# Revit family: LUXI_WATERPROOF LIGHT_HP-E
name_source: partatom
category: Apparecchi per illuminazione
revit_build: Autodesk Revit 2016 (Build: 20161004_0715(x64)
units: mm (PartAtom-declared; Revit-internal decimal feet)

## family parameters
Condiviso = No
Host = Superficie
Numero OmniClass = 23.80.70.00
Punto di calcolo locali = Sì
Quota connettore circolare = Usa diametro
Sorgente d'illuminazione = Sì
Taglio con vuoti quando caricato = No
Tipo di parte = Normale
Titolo OmniClass = Lighting

## types (10) — shared parameters
Alimentatore = Incluso
Alimentazione = 220-240V AC / 50-60 Hz
Angolo inclinazione = -90.00°
Certificazioni = CE / RohS
Classe di efficienza energetica = A+
Classe di protezione = I
Classe di rischio fotobiologico = Esente (RG0)
Colore = Grigio
Descrizione = Plafoniera Standard
Fattore di correzione di potenza = ≥0,95 (typ.)
Filtro dei colori = 16777215
Garanzia = 5 anni
Grado di protezione = IP 65 (frontale)
IFCExportAs = IfcLightFixtureType
Indice di resa cromatica = ≥80 (typ.)
Masterformat 2016 Codice = 26.50.00
Masterformat 2016 Descrizione = Lighting
Materiale 1 = Policarbonato V2_Grigio
Materiale 2 = Policarbonato V2 Diffondente
Materiale 3 = Policarbonato
Modello = Serie HP-E | Waterproof Light
Ottiche = Schermo policarbonato opalino riflettente
Produttore = Luxi Illuminazione S.r.l.
Prospetto di default = 2000 mm  [stored 6.56168 ft]
Protezione agli urti = IK10 (20 Joule)
Regolazione del flusso luminoso = Non disponibile
Rendi la forma visibile nel rendering = No
Revisione = 3
Sistema di illuminazione = Luce diretta
Sorgente = LED SMD
Step MacAdam (SDCM) = <4
Temperatura di esercizio = -40°C / +40°C
Tipologie di installazione = Sospensione / Parete / Soffitto
URL = https://www.luxi.lighting
Uniclass 2015 Codice = EF_70_80
Uniclass 2015 Descrizione = Lighting
Variazione temperatura colore lampada con luminosità attenuata = <Nessuno>
Vita utile = L70B20 50.000ore

## per-type parameters (varying)
| type | Carico apparente | Commenti sul tipo | Dimensioni | Emetti da larghezza rettangolo | Emetti da lunghezza rettangolo | File diagramma fotometrico | H | Larghezza | Lunghezza | Mod.1 | Mod.2 | Nota chiave | Peso | Potenza |
| WPHP020602G840 | 20 VA |  | 620x75x100 | 100 mm  [stored 0.328084 ft] | 620 mm  [stored 2.03412 ft] | WPHP020602G840 Luxi Serie HP-E 20W 4000K 600mm.IES | 75 mm | 100 mm  [stored 0.328084 ft] | 620 mm  [stored 2.03412 ft] | Sì | No |  | 1.20 kg | 20 W |
| WPHP040122G840 | 40 VA |  | 1220x75x100 | 100 mm  [stored 0.328084 ft] | 1220 mm  [stored 4.00262 ft] | WPHP040122G840 Luxi Serie HP-E 40W 4000K 1200mm.IES | 75 mm | 100 mm  [stored 0.328084 ft] | 1220 mm  [stored 4.00262 ft] | Sì | No |  | 2.20 kg | 40 W |
| WPHP030152G840 | 30 VA |  | 1520x75x100 | 100 mm  [stored 0.328084 ft] | 1520 mm | WPHP030152G840 Luxi Serie HP-E 30W 4000K 1500mm.IES | 75 mm | 100 mm  [stored 0.328084 ft] | 1520 mm | Sì | No |  | 2.80 kg | 30 W |
| WPHP060152G840 | 60 VA |  | 1520x75x100 | 100 mm  [stored 0.328084 ft] | 1520 mm | WPHP060152G840 Luxi Serie HP-E 60W 4000K 1500mm.IES | 75 mm | 100 mm  [stored 0.328084 ft] | 1520 mm | Sì | No |  | 2.80 kg | 60 W |
| WPHP060152G840P | 60 VA | Passante | 1520x75x100 | 100 mm  [stored 0.328084 ft] | 1520 mm | WPHP060152G840 Luxi Serie HP-E 60W 4000K 1500mm.IES | 75 mm | 100 mm  [stored 0.328084 ft] | 1520 mm | Sì | No |  | 2.80 kg | 60 W |
| WPHP020602G840E | 20 VA | Emergenza | 620x75x100 | 100 mm  [stored 0.328084 ft] | 620 mm  [stored 2.03412 ft] | WPHP020602G840 Luxi Serie HP-E 20W 4000K 600mm.IES | 75 mm | 100 mm  [stored 0.328084 ft] | 620 mm  [stored 2.03412 ft] | Sì | No | Autonomia 1h, ricarica 12h, SA 12W / 1400 lumen | 1.60 kg | 20 W |
| WPHP030152G840E | 30 VA | Emergenza | 1520x75x100 | 100 mm  [stored 0.328084 ft] | 1520 mm | WPHP030152G840 Luxi Serie HP-E 30W 4000K 1500mm.IES | 75 mm | 100 mm  [stored 0.328084 ft] | 1520 mm | Sì | No | Autonomia 1h, ricarica 12h, SA 12W / 1400 lumen | 3.20 kg | 30 W |
| WPHP040122G840E | 40 VA | Emergenza | 1220x75x100 | 100 mm  [stored 0.328084 ft] | 1220 mm  [stored 4.00262 ft] | WPHP040122G840 Luxi Serie HP-E 40W 4000K 1200mm.IES | 75 mm | 100 mm  [stored 0.328084 ft] | 1220 mm  [stored 4.00262 ft] | Sì | No | Autonomia 1h, ricarica 12h, SA 12W / 1400 lumen | 2.60 kg | 40 W |
| WPHP060152G840E | 60 VA | Emergenza | 1520x75x100 | 100 mm  [stored 0.328084 ft] | 1520 mm | WPHP060152G840 Luxi Serie HP-E 60W 4000K 1500mm.IES | 75 mm | 100 mm  [stored 0.328084 ft] | 1520 mm | Sì | No | Autonomia 1h, ricarica 12h, SA 12W / 1400 lumen | 3.20 kg | 60 W |
| WPHP060152G840DA | 60 VA | DALI | 1570x85x95 | 95 mm | 1570 mm | WPHP060150G840DA Luxi Serie HP-E 60W 4000K 1500mm DALI.IES | 85 mm  [stored 0.278871 ft] | 95 mm | 1570 mm | No | Sì |  | 2.80 kg | 60 W |

note: column(s) folded — value = type name in every type: Articolo

note: [stored X ft] marks values corroborated as IEEE doubles in the binary element streams (Revit-internal decimal feet)
